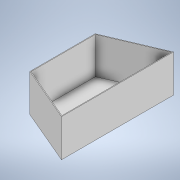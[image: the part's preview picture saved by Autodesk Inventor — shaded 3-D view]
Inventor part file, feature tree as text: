
AUTODESK INVENTOR PART (.ipt)
format: ipt  version: 2021 (Build 250183000, 183)  size: 99,328 bytes
history: native  units: mm
features: extrude x1, shell x1, sketch x1
ambient origin geometry x8: Origin, YZ Plane, XZ Plane, XY Plane, X Axis, Y Axis, Z Axis, Center Point
bodies: Solid1 (feature_tree)
feature tree (3):
  extrude  "Extrusion1"  Depth=81.25mm
  shell  "Shell1"  Thickness=11.693706mm
  sketch  "Sketch1"  dims[d5=152.4mm d6=81.25mm d7=11.693706mm d8=88.9mm d9=50.8mm d10=0.0mm d17=1.0mm]
